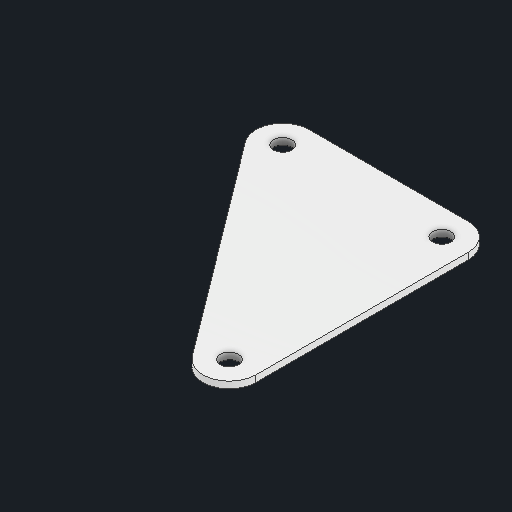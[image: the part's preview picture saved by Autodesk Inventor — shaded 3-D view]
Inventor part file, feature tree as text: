
AUTODESK INVENTOR PART (.ipt)
format: ipt  version: 2025 (Build 290162000, 162)  size: 129,536 bytes
history: native  units: in
note: dims shown in document units (in); Inventor stores cm internally (conversion verified against a paired STEP export)
features: other x4, extrude x1, sketch x1
ambient origin geometry x8: Origin, YZ Plane, XZ Plane, XY Plane, X Axis, Y Axis, Z Axis, Center Point
bodies: Solid1 (feature_tree)
feature tree (6):
  other  "Blocks"
  extrude  "Extrusion1"  Depth=0.0625in TaperAngle=0.0deg
  sketch  "Sketch1"  dims[d0=0.5in d1=0.5in d2=0.5in d3=0.0625in d4=0.0in]
  other  "main"
  other  "main:1"
  other  "Definition1"
